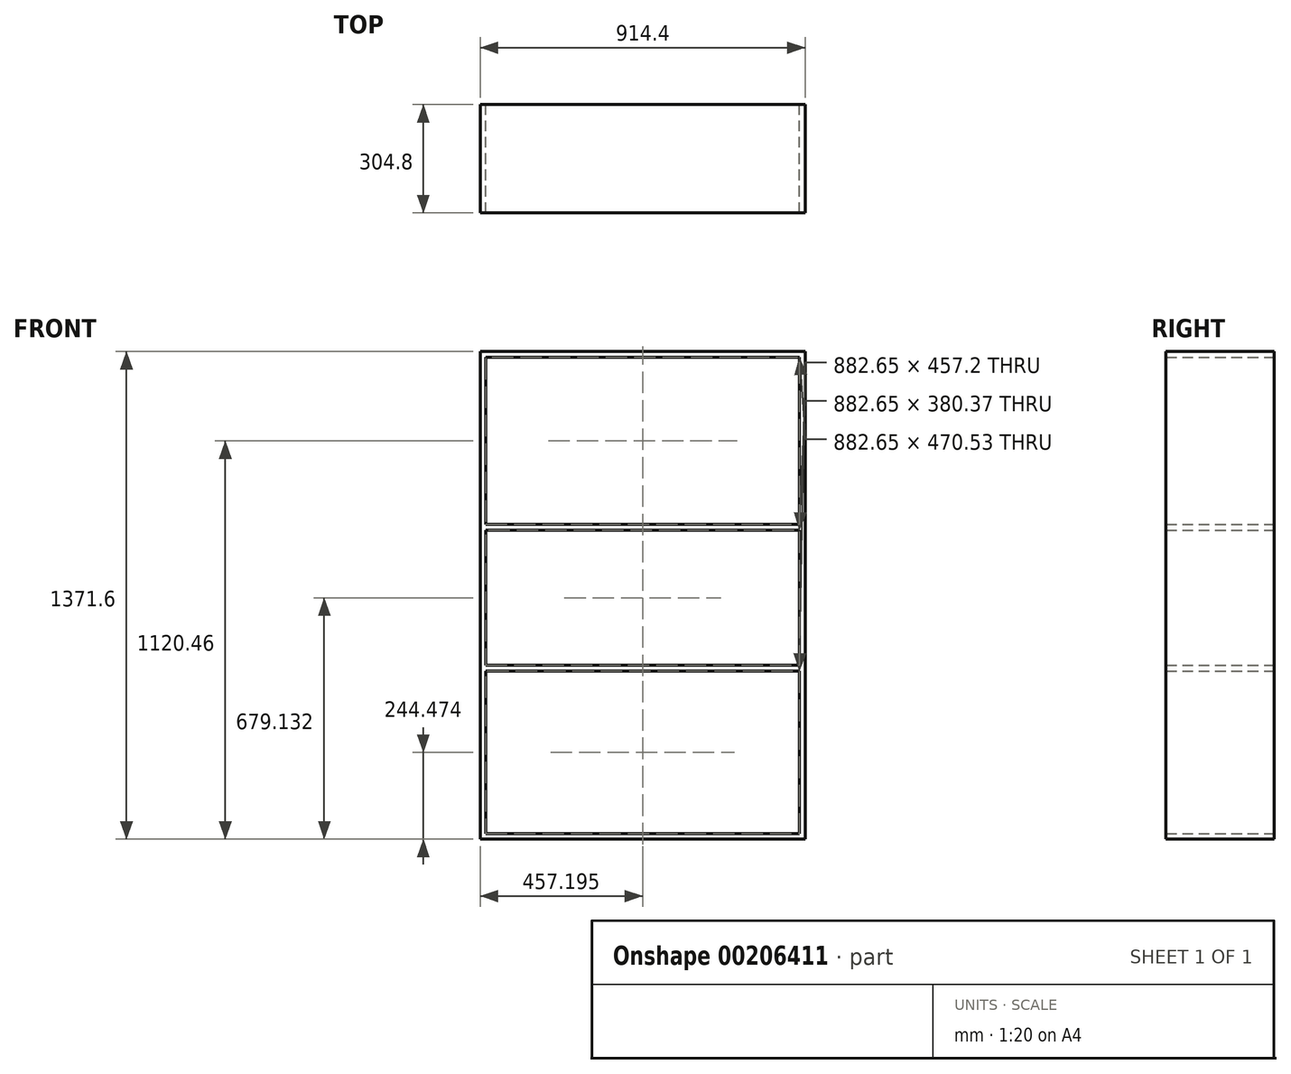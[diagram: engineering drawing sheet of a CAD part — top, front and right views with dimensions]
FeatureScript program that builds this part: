
annotation { "Feature Type Name" : "Feature", "Feature Type Description" : "" }
export const myFeature = defineFeature(function(context is Context, id is Id, definition is map)
    precondition{}
    {
        {
            var Q0;
            Q0=qCreatedBy(makeId("Front.planeOp"),FACE);
            var sketch = newSketch(context, id + "F0", { "sketchPlane" : qUnion([Q0])});
            skLineSegment(sketch, "E0.bottom", {"start": v(-769.9, 643.74) * mm, "end": v(144.5, 643.74) * mm});
            skLineSegment(sketch, "E0.top", {"start": v(-769.9, -727.86) * mm, "end": v(144.5, -727.86) * mm});
            skLineSegment(sketch, "E0.left", {"start": v(-769.9, 643.74) * mm, "end": v(-769.9, -727.86) * mm});
            skLineSegment(sketch, "E0.right", {"start": v(144.5, 643.74) * mm, "end": v(144.5, -727.86) * mm});
            skLineSegment(sketch, "E1.bottom", {"start": v(-754.03, 627.86) * mm, "end": v(128.62, 627.86) * mm});
            skLineSegment(sketch, "E1.top", {"start": v(-754.03, -711.99) * mm, "end": v(128.62, -711.99) * mm});
            skLineSegment(sketch, "E1.left", {"start": v(-754.03, 627.86) * mm, "end": v(-754.03, -711.99) * mm});
            skLineSegment(sketch, "E1.right", {"start": v(128.62, 627.86) * mm, "end": v(128.62, -711.99) * mm});
            skLineSegment(sketch, "E2.bottom", {"start": v(-754.03, -238.91) * mm, "end": v(128.62, -238.91) * mm});
            skLineSegment(sketch, "E2.top", {"start": v(-754.03, -254.79) * mm, "end": v(128.62, -254.79) * mm});
            skLineSegment(sketch, "E2.left", {"start": v(-754.03, -238.91) * mm, "end": v(-754.03, -254.79) * mm});
            skLineSegment(sketch, "E2.right", {"start": v(128.62, -238.91) * mm, "end": v(128.62, -254.79) * mm});
            skLineSegment(sketch, "E3.0.1.0", {"start": v(-754.03, 141.45) * mm, "end": v(128.62, 141.45) * mm});
            skLineSegment(sketch, "E3.0.1.1", {"start": v(-754.03, 157.33) * mm, "end": v(128.62, 157.33) * mm});
            skLineSegment(sketch, "E3.direction1", {"start": v(-754.03, -254.79) * mm, "end": v(-729.03, -254.79) * mm, "construction": true});
            skLineSegment(sketch, "E3.direction2", {"start": v(-754.03, -254.79) * mm, "end": v(-754.03, 141.45) * mm, "construction": true});
            skSolve(sketch);
        }
        {
            var Q0;
            Q0 = qSketchRegion(id + "F0", true);
            var Q1;
            {var subQ0=sQuery(id+"F0.wireOp",EDGE,"E3.0.1.0");Q1=makeQuery(id+"F0.imprint","IMPRINT",FACE,{"disambiguationData":[TD([[makeQuery(id+"F0.imprint","IMPRINT",EDGE,{"derivedFrom":subQ0}),1.0]])]});}
            var Q2;
            Q2=makeQuery(id+"F0.imprint","IMPRINT",FACE,{"disambiguationData":[TD([[makeQuery(id+"F0.imprint","IMPRINT",EDGE,{"derivedFrom":sQuery(id+"F0.wireOp",EDGE,"E2.bottom")}),-1.0]])]});
            extrude(context, id + "F1", {"entities" : qUnion([Q0, Q1, Q2]), "depth" : 304.8 * mm});
        }
    });
